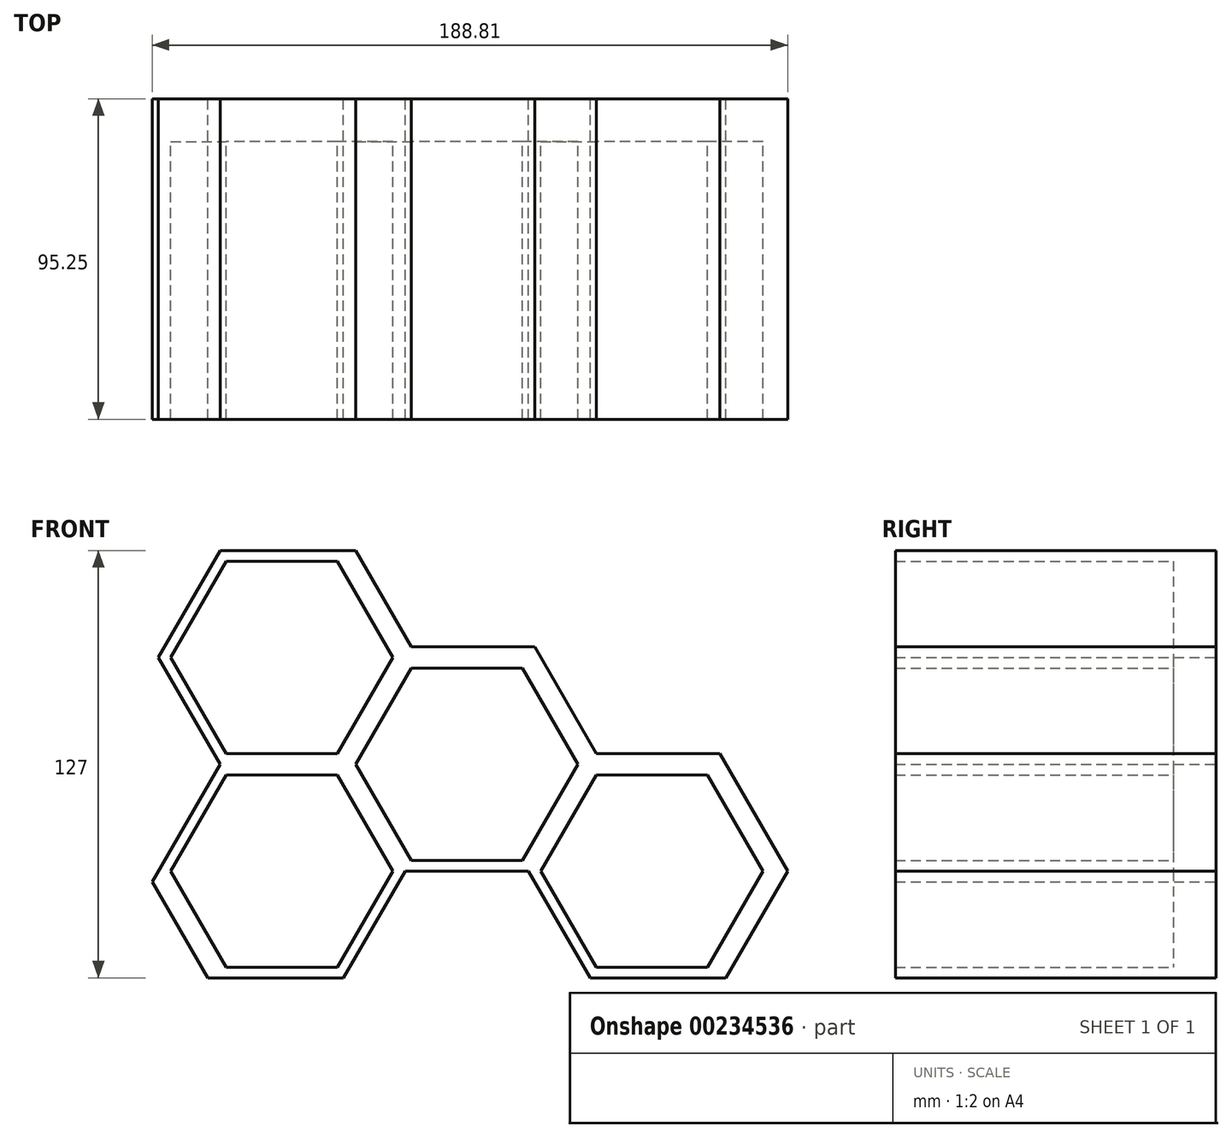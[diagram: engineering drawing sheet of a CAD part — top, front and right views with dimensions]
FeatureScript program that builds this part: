
annotation { "Feature Type Name" : "Feature", "Feature Type Description" : "" }
export const myFeature = defineFeature(function(context is Context, id is Id, definition is map)
    precondition{}
    {
        {
            var Q0;
            Q0=qCreatedBy(makeId("Front.planeOp"),FACE);
            var sketch = newSketch(context, id + "F0", { "sketchPlane" : qUnion([Q0])});
            skLineSegment(sketch, "E0.2", {"start": v(32.38, 98.54) * mm, "end": v(50.71, 66.8) * mm});
            skLineSegment(sketch, "E0.3", {"start": v(50.71, 66.8) * mm, "end": v(32.38, 35.04) * mm});
            skLineSegment(sketch, "E1.3", {"start": v(50.71, 130.3) * mm, "end": v(32.38, 98.54) * mm});
            skLineSegment(sketch, "E2.4", {"start": v(87.38, 130.3) * mm, "end": v(50.71, 130.3) * mm});
            skCircle(sketch, "E3.cCircle", {"center": v(69.05, 98.54) * mm, "radius": 28.58 * mm, "construction": true});
            skLineSegment(sketch, "E3.0", {"start": v(36.05, 98.54) * mm, "end": v(52.55, 127.12) * mm});
            skLineSegment(sketch, "E3.1", {"start": v(52.55, 127.12) * mm, "end": v(85.54, 127.12) * mm});
            skLineSegment(sketch, "E3.2", {"start": v(85.54, 127.12) * mm, "end": v(102.04, 98.54) * mm});
            skLineSegment(sketch, "E3.3", {"start": v(102.04, 98.54) * mm, "end": v(85.54, 69.97) * mm});
            skLineSegment(sketch, "E3.4", {"start": v(85.54, 69.97) * mm, "end": v(52.55, 69.97) * mm});
            skLineSegment(sketch, "E3.5", {"start": v(52.55, 69.97) * mm, "end": v(36.05, 98.54) * mm});
            skPoint(sketch, "E3.0.midPoint", {"position": v(44.3, 112.83) * mm});
            skCircle(sketch, "E4.cCircle", {"center": v(69.05, 98.54) * mm, "radius": 31.75 * mm, "construction": true});
            skLineSegment(sketch, "E4.0", {"start": v(32.38, 98.54) * mm, "end": v(50.71, 130.3) * mm});
            skLineSegment(sketch, "E4.1", {"start": v(50.71, 130.3) * mm, "end": v(87.38, 130.3) * mm});
            skLineSegment(sketch, "E4.2", {"start": v(87.38, 130.3) * mm, "end": v(105.7, 98.54) * mm});
            skLineSegment(sketch, "E4.3", {"start": v(105.7, 98.54) * mm, "end": v(87.38, 66.8) * mm});
            skLineSegment(sketch, "E4.4", {"start": v(87.38, 66.8) * mm, "end": v(50.71, 66.8) * mm});
            skLineSegment(sketch, "E4.5", {"start": v(50.71, 66.8) * mm, "end": v(32.38, 98.54) * mm});
            skPoint(sketch, "E4.0.midPoint", {"position": v(41.55, 114.42) * mm});
            skCircle(sketch, "E5.cCircle", {"center": v(69.05, 35.04) * mm, "radius": 28.58 * mm, "construction": true});
            skLineSegment(sketch, "E5.0", {"start": v(36.05, 35.04) * mm, "end": v(52.55, 63.62) * mm});
            skLineSegment(sketch, "E5.1", {"start": v(52.55, 63.62) * mm, "end": v(85.54, 63.62) * mm});
            skLineSegment(sketch, "E5.2", {"start": v(85.54, 63.62) * mm, "end": v(102.04, 35.04) * mm});
            skLineSegment(sketch, "E5.3", {"start": v(102.04, 35.04) * mm, "end": v(85.54, 6.47) * mm});
            skLineSegment(sketch, "E5.4", {"start": v(85.54, 6.47) * mm, "end": v(52.55, 6.47) * mm});
            skLineSegment(sketch, "E5.5", {"start": v(52.55, 6.47) * mm, "end": v(36.05, 35.04) * mm});
            skPoint(sketch, "E5.0.midPoint", {"position": v(44.3, 49.33) * mm});
            skCircle(sketch, "E6.cCircle", {"center": v(69.05, 35.04) * mm, "radius": 31.75 * mm, "construction": true});
            skLineSegment(sketch, "E6.0", {"start": v(32.38, 35.04) * mm, "end": v(50.71, 66.8) * mm});
            skLineSegment(sketch, "E6.1", {"start": v(50.71, 66.8) * mm, "end": v(87.38, 66.8) * mm});
            skLineSegment(sketch, "E6.2", {"start": v(87.38, 66.8) * mm, "end": v(105.7, 35.04) * mm});
            skLineSegment(sketch, "E6.3", {"start": v(105.7, 35.04) * mm, "end": v(87.38, 3.3) * mm});
            skLineSegment(sketch, "E6.4", {"start": v(87.38, 3.3) * mm, "end": v(50.71, 3.3) * mm});
            skLineSegment(sketch, "E6.5", {"start": v(50.71, 3.3) * mm, "end": v(32.38, 35.04) * mm});
            skPoint(sketch, "E6.0.midPoint", {"position": v(41.55, 50.92) * mm});
            skLineSegment(sketch, "E7.1", {"start": v(50.71, 3.3) * mm, "end": v(87.38, 3.3) * mm});
            skLineSegment(sketch, "E8.0", {"start": v(87.38, 3.3) * mm, "end": v(105.7, 35.04) * mm});
            skLineSegment(sketch, "E8.1", {"start": v(105.7, 35.04) * mm, "end": v(142.37, 35.04) * mm});
            skLineSegment(sketch, "E8.2", {"start": v(142.37, 35.04) * mm, "end": v(160.7, 3.3) * mm});
            skPoint(sketch, "E8.0.midPoint", {"position": v(96.54, 19.17) * mm});
            skCircle(sketch, "E9.cCircle", {"center": v(124.04, 66.8) * mm, "radius": 28.58 * mm, "construction": true});
            skLineSegment(sketch, "E9.0", {"start": v(91.04, 66.8) * mm, "end": v(107.54, 95.37) * mm});
            skLineSegment(sketch, "E9.1", {"start": v(107.54, 95.37) * mm, "end": v(140.54, 95.37) * mm});
            skLineSegment(sketch, "E9.2", {"start": v(140.54, 95.37) * mm, "end": v(157.03, 66.8) * mm});
            skLineSegment(sketch, "E9.3", {"start": v(157.03, 66.8) * mm, "end": v(140.54, 38.22) * mm});
            skLineSegment(sketch, "E9.4", {"start": v(140.54, 38.22) * mm, "end": v(107.54, 38.22) * mm});
            skLineSegment(sketch, "E9.5", {"start": v(107.54, 38.22) * mm, "end": v(91.04, 66.8) * mm});
            skPoint(sketch, "E9.0.midPoint", {"position": v(99.3, 81.08) * mm});
            skCircle(sketch, "E10.cCircle", {"center": v(124.04, 66.8) * mm, "radius": 31.75 * mm, "construction": true});
            skLineSegment(sketch, "E10.0", {"start": v(87.38, 66.8) * mm, "end": v(105.7, 98.54) * mm});
            skLineSegment(sketch, "E10.1", {"start": v(105.7, 98.54) * mm, "end": v(142.37, 98.54) * mm});
            skLineSegment(sketch, "E10.2", {"start": v(142.37, 98.54) * mm, "end": v(160.7, 66.8) * mm});
            skLineSegment(sketch, "E10.3", {"start": v(160.7, 66.8) * mm, "end": v(142.37, 35.04) * mm});
            skLineSegment(sketch, "E10.4", {"start": v(142.37, 35.04) * mm, "end": v(105.7, 35.04) * mm});
            skLineSegment(sketch, "E10.5", {"start": v(105.7, 35.04) * mm, "end": v(87.38, 66.8) * mm});
            skPoint(sketch, "E10.0.midPoint", {"position": v(96.54, 82.67) * mm});
            skLineSegment(sketch, "E11.1", {"start": v(160.7, 3.3) * mm, "end": v(197.36, 3.3) * mm});
            skCircle(sketch, "E12.cCircle", {"center": v(179.03, 35.04) * mm, "radius": 28.58 * mm, "construction": true});
            skLineSegment(sketch, "E12.0", {"start": v(146.03, 35.04) * mm, "end": v(162.53, 63.62) * mm});
            skLineSegment(sketch, "E12.1", {"start": v(162.53, 63.62) * mm, "end": v(195.53, 63.62) * mm});
            skLineSegment(sketch, "E12.2", {"start": v(195.53, 63.62) * mm, "end": v(212.03, 35.04) * mm});
            skLineSegment(sketch, "E12.3", {"start": v(212.03, 35.04) * mm, "end": v(195.53, 6.47) * mm});
            skLineSegment(sketch, "E12.4", {"start": v(195.53, 6.47) * mm, "end": v(162.53, 6.47) * mm});
            skLineSegment(sketch, "E12.5", {"start": v(162.53, 6.47) * mm, "end": v(146.03, 35.04) * mm});
            skPoint(sketch, "E12.0.midPoint", {"position": v(154.28, 49.33) * mm});
            skCircle(sketch, "E13.cCircle", {"center": v(179.03, 35.04) * mm, "radius": 31.75 * mm, "construction": true});
            skLineSegment(sketch, "E13.0", {"start": v(142.37, 35.04) * mm, "end": v(160.7, 66.8) * mm});
            skLineSegment(sketch, "E13.1", {"start": v(160.7, 66.8) * mm, "end": v(197.36, 66.8) * mm});
            skLineSegment(sketch, "E13.2", {"start": v(197.36, 66.8) * mm, "end": v(215.7, 35.04) * mm});
            skLineSegment(sketch, "E13.3", {"start": v(215.7, 35.04) * mm, "end": v(197.36, 3.3) * mm});
            skLineSegment(sketch, "E13.4", {"start": v(197.36, 3.3) * mm, "end": v(160.7, 3.3) * mm});
            skLineSegment(sketch, "E13.5", {"start": v(160.7, 3.3) * mm, "end": v(142.37, 35.04) * mm});
            skPoint(sketch, "E13.0.midPoint", {"position": v(151.53, 50.92) * mm});
            skLineSegment(sketch, "E14", {"start": v(30.55, 31.87) * mm, "end": v(47.05, 3.3) * mm});
            skLineSegment(sketch, "E15", {"start": v(201.03, 3.3) * mm, "end": v(219.36, 35.04) * mm});
            skLineSegment(sketch, "E16", {"start": v(219.36, 35.04) * mm, "end": v(199.2, 69.97) * mm});
            skLineSegment(sketch, "E17", {"start": v(199.2, 69.97) * mm, "end": v(162.53, 69.97) * mm});
            skLineSegment(sketch, "E18", {"start": v(162.53, 69.97) * mm, "end": v(144.2, 101.72) * mm});
            skLineSegment(sketch, "E19", {"start": v(144.2, 101.72) * mm, "end": v(107.54, 101.72) * mm});
            skLineSegment(sketch, "E20", {"start": v(107.54, 101.72) * mm, "end": v(91.04, 130.3) * mm});
            skLineSegment(sketch, "E21", {"start": v(47.05, 3.3) * mm, "end": v(50.71, 3.3) * mm});
            skLineSegment(sketch, "E22", {"start": v(32.38, 35.04) * mm, "end": v(30.55, 31.87) * mm});
            skLineSegment(sketch, "E23", {"start": v(91.04, 130.3) * mm, "end": v(87.38, 130.3) * mm});
            skLineSegment(sketch, "E24", {"start": v(201.03, 3.3) * mm, "end": v(197.36, 3.3) * mm});
            skSolve(sketch);
        }
        {
            var Q0;
            Q0=makeQuery(id+"F0.imprint","IMPRINT",FACE,{"disambiguationData":[TD([[makeQuery(id+"F0.imprint","IMPRINT",EDGE,{"derivedFrom":sQuery(id+"F0.wireOp",EDGE,"68d16a58-0471-4e1c-b2b3-2a61df7c0d9d.0")}),-1.0]])]});
            var Q1;
            Q1=makeQuery(id+"F0.imprint","IMPRINT",FACE,{"disambiguationData":[TD([[makeQuery(id+"F0.imprint","IMPRINT",EDGE,{"derivedFrom":sQuery(id+"F0.wireOp",EDGE,"ae29455d-c252-400a-b569-c5a1c48e1351.0")}),-1.0]])]});
            var Q2;
            Q2=makeQuery(id+"F0.imprint","IMPRINT",FACE,{"disambiguationData":[TD([[makeQuery(id+"F0.imprint","IMPRINT",EDGE,{"derivedFrom":sQuery(id+"F0.wireOp",EDGE,"cad1e4f3-bd43-45ec-b31a-1d5006939c94.0")}),-1.0]])]});
            var Q3;
            Q3=makeQuery(id+"F0.imprint","IMPRINT",FACE,{"disambiguationData":[TD([[makeQuery(id+"F0.imprint","IMPRINT",EDGE,{"derivedFrom":sQuery(id+"F0.wireOp",EDGE,"b43d4d8c-f78a-4ff8-8565-99a66ce6ec5f.0")}),-1.0]])]});
            var Q4;
            Q4=makeQuery(id+"F0.imprint","IMPRINT",FACE,{"disambiguationData":[TD([[makeQuery(id+"F0.imprint","IMPRINT",EDGE,{"derivedFrom":sQuery(id+"F0.wireOp",EDGE,"E3.0")}),-1.0]])]});
            var Q5;
            Q5=makeQuery(id+"F0.imprint","IMPRINT",FACE,{"disambiguationData":[TD([[makeQuery(id+"F0.imprint","IMPRINT",EDGE,{"derivedFrom":sQuery(id+"F0.wireOp",EDGE,"E5.0")}),-1.0]])]});
            var Q6;
            Q6=makeQuery(id+"F0.imprint","IMPRINT",FACE,{"disambiguationData":[TD([[makeQuery(id+"F0.imprint","IMPRINT",EDGE,{"derivedFrom":sQuery(id+"F0.wireOp",EDGE,"0bf0733b-7d93-4c2e-8366-56d2cde24658.0")}),-1.0]])]});
            var Q7;
            Q7=makeQuery(id+"F0.imprint","IMPRINT",FACE,{"disambiguationData":[TD([[makeQuery(id+"F0.imprint","IMPRINT",EDGE,{"derivedFrom":sQuery(id+"F0.wireOp",EDGE,"93717492-86db-456f-ae55-f71e4e93837b.0")}),-1.0]])]});
            var Q8;
            Q8=makeQuery(id+"F0.imprint","IMPRINT",FACE,{"disambiguationData":[TD([[makeQuery(id+"F0.imprint","IMPRINT",EDGE,{"derivedFrom":sQuery(id+"F0.wireOp",EDGE,"f16ea8c9-6b67-4651-8441-f7eb3c0ce7d7.0")}),-1.0]])]});
            var Q9;
            Q9=makeQuery(id+"F0.imprint","IMPRINT",FACE,{"disambiguationData":[TD([[makeQuery(id+"F0.imprint","IMPRINT",EDGE,{"derivedFrom":sQuery(id+"F0.wireOp",EDGE,"0306a0a6-7289-4661-a415-5fa5585f2cb5.0")}),-1.0]])]});
            var Q10;
            Q10=makeQuery(id+"F0.imprint","IMPRINT",FACE,{"disambiguationData":[TD([[makeQuery(id+"F0.imprint","IMPRINT",EDGE,{"derivedFrom":sQuery(id+"F0.wireOp",EDGE,"0a91a14e-ea0c-483f-91eb-c48bd73cb0e6.0")}),-1.0]])]});
            var Q11;
            Q11=makeQuery(id+"F0.imprint","IMPRINT",FACE,{"disambiguationData":[TD([[makeQuery(id+"F0.imprint","IMPRINT",EDGE,{"derivedFrom":sQuery(id+"F0.wireOp",EDGE,"cbfd9497-f7fe-4f18-9288-d90aa8075d81.0")}),-1.0]])]});
            var Q12;
            Q12=makeQuery(id+"F0.imprint","IMPRINT",FACE,{"disambiguationData":[TD([[makeQuery(id+"F0.imprint","IMPRINT",EDGE,{"derivedFrom":sQuery(id+"F0.wireOp",EDGE,"6282d196-dd8f-4bb0-bca4-b9108e277473.0")}),-1.0]])]});
            var Q13;
            Q13=makeQuery(id+"F0.imprint","IMPRINT",FACE,{"disambiguationData":[TD([[makeQuery(id+"F0.imprint","IMPRINT",EDGE,{"derivedFrom":sQuery(id+"F0.wireOp",EDGE,"084ca30c-4dc0-463f-bfd9-557787ed9a2f.0")}),-1.0]])]});
            var Q14;
            Q14=makeQuery(id+"F0.imprint","IMPRINT",FACE,{"disambiguationData":[TD([[makeQuery(id+"F0.imprint","IMPRINT",EDGE,{"derivedFrom":sQuery(id+"F0.wireOp",EDGE,"E12.0")}),-1.0]])]});
            var Q15;
            Q15=makeQuery(id+"F0.imprint","IMPRINT",FACE,{"disambiguationData":[TD([[makeQuery(id+"F0.imprint","IMPRINT",EDGE,{"derivedFrom":sQuery(id+"F0.wireOp",EDGE,"b8eec94e-d97e-439b-aaac-63499233db4c.0")}),-1.0]])]});
            var Q16;
            Q16=makeQuery(id+"F0.imprint","IMPRINT",FACE,{"disambiguationData":[TD([[makeQuery(id+"F0.imprint","IMPRINT",EDGE,{"derivedFrom":sQuery(id+"F0.wireOp",EDGE,"2e929887-9bb9-4083-9cef-f9a6a24e8e46.0")}),-1.0]])]});
            var Q17;
            Q17=makeQuery(id+"F0.imprint","IMPRINT",FACE,{"disambiguationData":[TD([[makeQuery(id+"F0.imprint","IMPRINT",EDGE,{"derivedFrom":sQuery(id+"F0.wireOp",EDGE,"23671680-92ab-419e-a071-eb0943a5012b.0")}),-1.0]])]});
            var Q18;
            Q18=makeQuery(id+"F0.imprint","IMPRINT",FACE,{"disambiguationData":[TD([[makeQuery(id+"F0.imprint","IMPRINT",EDGE,{"derivedFrom":sQuery(id+"F0.wireOp",EDGE,"a1daa6ae-7864-4614-8fb9-3511dddc1266.0")}),-1.0]])]});
            var Q19;
            Q19=makeQuery(id+"F0.imprint","IMPRINT",FACE,{"disambiguationData":[TD([[makeQuery(id+"F0.imprint","IMPRINT",EDGE,{"derivedFrom":sQuery(id+"F0.wireOp",EDGE,"37efd634-c264-4683-8864-08b38c7986ca.0")}),-1.0]])]});
            var Q20;
            Q20=makeQuery(id+"F0.imprint","IMPRINT",FACE,{"disambiguationData":[TD([[makeQuery(id+"F0.imprint","IMPRINT",EDGE,{"derivedFrom":sQuery(id+"F0.wireOp",EDGE,"E9.0")}),-1.0]])]});
            var Q21;
            Q21=makeQuery(id+"F0.imprint","IMPRINT",FACE,{"disambiguationData":[TD([[makeQuery(id+"F0.imprint","IMPRINT",EDGE,{"derivedFrom":sQuery(id+"F0.wireOp",EDGE,"1f2aec04-a318-49b9-a42e-ea2fce35ed6c.0")}),-1.0]])]});
            var Q22;
            Q22=makeQuery(id+"F0.imprint","IMPRINT",FACE,{"disambiguationData":[TD([[makeQuery(id+"F0.imprint","IMPRINT",EDGE,{"derivedFrom":sQuery(id+"F0.wireOp",EDGE,"f97fdbdd-69fc-44f1-b8f7-f6a6a25558e6.0")}),-1.0]])]});
            var Q23;
            Q23=makeQuery(id+"F0.imprint","IMPRINT",FACE,{"disambiguationData":[TD([[makeQuery(id+"F0.imprint","IMPRINT",EDGE,{"derivedFrom":sQuery(id+"F0.wireOp",EDGE,"4e92e904-9607-490d-a429-b319c41500d9.0")}),-1.0]])]});
            var Q24;
            Q24=makeQuery(id+"F0.imprint","IMPRINT",FACE,{"disambiguationData":[TD([[makeQuery(id+"F0.imprint","IMPRINT",EDGE,{"derivedFrom":sQuery(id+"F0.wireOp",EDGE,"084ca30c-4dc0-463f-bfd9-557787ed9a2f.0")}),1.0]])]});
            var Q25;
            Q25=makeQuery(id+"F0.imprint","IMPRINT",FACE,{"disambiguationData":[TD([[makeQuery(id+"F0.imprint","IMPRINT",EDGE,{"derivedFrom":sQuery(id+"F0.wireOp",EDGE,"1f2aec04-a318-49b9-a42e-ea2fce35ed6c.0")}),1.0]])]});
            var Q26;
            Q26=makeQuery(id+"F0.imprint","IMPRINT",FACE,{"disambiguationData":[TD([[makeQuery(id+"F0.imprint","IMPRINT",EDGE,{"derivedFrom":sQuery(id+"F0.wireOp",EDGE,"23671680-92ab-419e-a071-eb0943a5012b.0")}),1.0]])]});
            var Q27;
            Q27=makeQuery(id+"F0.imprint","IMPRINT",FACE,{"disambiguationData":[TD([[makeQuery(id+"F0.imprint","IMPRINT",EDGE,{"derivedFrom":sQuery(id+"F0.wireOp",EDGE,"2e929887-9bb9-4083-9cef-f9a6a24e8e46.0")}),1.0]])]});
            var Q28;
            Q28=makeQuery(id+"F0.imprint","IMPRINT",FACE,{"disambiguationData":[TD([[makeQuery(id+"F0.imprint","IMPRINT",EDGE,{"derivedFrom":sQuery(id+"F0.wireOp",EDGE,"4e92e904-9607-490d-a429-b319c41500d9.0")}),1.0]])]});
            var Q29;
            Q29=makeQuery(id+"F0.imprint","IMPRINT",FACE,{"disambiguationData":[TD([[makeQuery(id+"F0.imprint","IMPRINT",EDGE,{"derivedFrom":sQuery(id+"F0.wireOp",EDGE,"b43d4d8c-f78a-4ff8-8565-99a66ce6ec5f.0")}),1.0]])]});
            var Q30;
            Q30=makeQuery(id+"F0.imprint","IMPRINT",FACE,{"disambiguationData":[TD([[makeQuery(id+"F0.imprint","IMPRINT",EDGE,{"derivedFrom":sQuery(id+"F0.wireOp",EDGE,"ae29455d-c252-400a-b569-c5a1c48e1351.0")}),1.0]])]});
            var Q31;
            Q31=makeQuery(id+"F0.imprint","IMPRINT",FACE,{"disambiguationData":[TD([[makeQuery(id+"F0.imprint","IMPRINT",EDGE,{"derivedFrom":sQuery(id+"F0.wireOp",EDGE,"0a91a14e-ea0c-483f-91eb-c48bd73cb0e6.0")}),1.0]])]});
            var Q32;
            Q32=makeQuery(id+"F0.imprint","IMPRINT",FACE,{"disambiguationData":[TD([[makeQuery(id+"F0.imprint","IMPRINT",EDGE,{"derivedFrom":sQuery(id+"F0.wireOp",EDGE,"E5.0")}),1.0]])]});
            var Q33;
            Q33=makeQuery(id+"F0.imprint","IMPRINT",FACE,{"disambiguationData":[TD([[makeQuery(id+"F0.imprint","IMPRINT",EDGE,{"derivedFrom":sQuery(id+"F0.wireOp",EDGE,"cbfd9497-f7fe-4f18-9288-d90aa8075d81.0")}),1.0]])]});
            var Q34;
            Q34=makeQuery(id+"F0.imprint","IMPRINT",FACE,{"disambiguationData":[TD([[makeQuery(id+"F0.imprint","IMPRINT",EDGE,{"derivedFrom":sQuery(id+"F0.wireOp",EDGE,"f97fdbdd-69fc-44f1-b8f7-f6a6a25558e6.0")}),1.0]])]});
            var Q35;
            Q35=makeQuery(id+"F0.imprint","IMPRINT",FACE,{"disambiguationData":[TD([[makeQuery(id+"F0.imprint","IMPRINT",EDGE,{"derivedFrom":sQuery(id+"F0.wireOp",EDGE,"b8eec94e-d97e-439b-aaac-63499233db4c.0")}),1.0]])]});
            var Q36;
            Q36=makeQuery(id+"F0.imprint","IMPRINT",FACE,{"disambiguationData":[TD([[makeQuery(id+"F0.imprint","IMPRINT",EDGE,{"derivedFrom":sQuery(id+"F0.wireOp",EDGE,"E3.0")}),1.0]])]});
            var Q37;
            Q37=makeQuery(id+"F0.imprint","IMPRINT",FACE,{"disambiguationData":[TD([[makeQuery(id+"F0.imprint","IMPRINT",EDGE,{"derivedFrom":sQuery(id+"F0.wireOp",EDGE,"f16ea8c9-6b67-4651-8441-f7eb3c0ce7d7.0")}),1.0]])]});
            var Q38;
            Q38=makeQuery(id+"F0.imprint","IMPRINT",FACE,{"disambiguationData":[TD([[makeQuery(id+"F0.imprint","IMPRINT",EDGE,{"derivedFrom":sQuery(id+"F0.wireOp",EDGE,"37efd634-c264-4683-8864-08b38c7986ca.0")}),1.0]])]});
            var Q39;
            Q39=makeQuery(id+"F0.imprint","IMPRINT",FACE,{"disambiguationData":[TD([[makeQuery(id+"F0.imprint","IMPRINT",EDGE,{"derivedFrom":sQuery(id+"F0.wireOp",EDGE,"68d16a58-0471-4e1c-b2b3-2a61df7c0d9d.0")}),1.0]])]});
            var Q40;
            Q40=makeQuery(id+"F0.imprint","IMPRINT",FACE,{"disambiguationData":[TD([[makeQuery(id+"F0.imprint","IMPRINT",EDGE,{"derivedFrom":sQuery(id+"F0.wireOp",EDGE,"0306a0a6-7289-4661-a415-5fa5585f2cb5.0")}),1.0]])]});
            var Q41;
            Q41=makeQuery(id+"F0.imprint","IMPRINT",FACE,{"disambiguationData":[TD([[makeQuery(id+"F0.imprint","IMPRINT",EDGE,{"derivedFrom":sQuery(id+"F0.wireOp",EDGE,"0bf0733b-7d93-4c2e-8366-56d2cde24658.0")}),1.0]])]});
            var Q42;
            Q42=makeQuery(id+"F0.imprint","IMPRINT",FACE,{"disambiguationData":[TD([[makeQuery(id+"F0.imprint","IMPRINT",EDGE,{"derivedFrom":sQuery(id+"F0.wireOp",EDGE,"E12.0")}),1.0]])]});
            var Q43;
            Q43=makeQuery(id+"F0.imprint","IMPRINT",FACE,{"disambiguationData":[TD([[makeQuery(id+"F0.imprint","IMPRINT",EDGE,{"derivedFrom":sQuery(id+"F0.wireOp",EDGE,"6282d196-dd8f-4bb0-bca4-b9108e277473.0")}),1.0]])]});
            var Q44;
            Q44=makeQuery(id+"F0.imprint","IMPRINT",FACE,{"disambiguationData":[TD([[makeQuery(id+"F0.imprint","IMPRINT",EDGE,{"derivedFrom":sQuery(id+"F0.wireOp",EDGE,"cad1e4f3-bd43-45ec-b31a-1d5006939c94.0")}),1.0]])]});
            var Q45;
            Q45=makeQuery(id+"F0.imprint","IMPRINT",FACE,{"disambiguationData":[TD([[makeQuery(id+"F0.imprint","IMPRINT",EDGE,{"derivedFrom":sQuery(id+"F0.wireOp",EDGE,"E9.0")}),1.0]])]});
            var Q46;
            Q46=makeQuery(id+"F0.imprint","IMPRINT",FACE,{"disambiguationData":[TD([[makeQuery(id+"F0.imprint","IMPRINT",EDGE,{"derivedFrom":sQuery(id+"F0.wireOp",EDGE,"a1daa6ae-7864-4614-8fb9-3511dddc1266.0")}),1.0]])]});
            var Q47;
            Q47=makeQuery(id+"F0.imprint","IMPRINT",FACE,{"disambiguationData":[TD([[makeQuery(id+"F0.imprint","IMPRINT",EDGE,{"derivedFrom":sQuery(id+"F0.wireOp",EDGE,"93717492-86db-456f-ae55-f71e4e93837b.0")}),1.0]])]});
            extrude(context, id + "F1", {"entities" : qUnion([Q0, Q1, Q2, Q3, Q4, Q5, Q6, Q7, Q8, Q9, Q10, Q11, Q12, Q13, Q14, Q15, Q16, Q17, Q18, Q19, Q20, Q21, Q22, Q23, Q24, Q25, Q26, Q27, Q28, Q29, Q30, Q31, Q32, Q33, Q34, Q35, Q36, Q37, Q38, Q39, Q40, Q41, Q42, Q43, Q44, Q45, Q46, Q47]), "depth" : 12.7 * mm});
        }
        {
            var Q0;
            Q0=makeQuery(id+"F0.imprint","IMPRINT",FACE,{"disambiguationData":[TD([[makeQuery(id+"F0.imprint","IMPRINT",EDGE,{"derivedFrom":sQuery(id+"F0.wireOp",EDGE,"E3.0")}),1.0]])]});
            var Q1;
            Q1=makeQuery(id+"F0.imprint","IMPRINT",FACE,{"disambiguationData":[TD([[makeQuery(id+"F0.imprint","IMPRINT",EDGE,{"derivedFrom":sQuery(id+"F0.wireOp",EDGE,"b8eec94e-d97e-439b-aaac-63499233db4c.0")}),1.0]])]});
            var Q2;
            Q2=makeQuery(id+"F0.imprint","IMPRINT",FACE,{"disambiguationData":[TD([[makeQuery(id+"F0.imprint","IMPRINT",EDGE,{"derivedFrom":sQuery(id+"F0.wireOp",EDGE,"cad1e4f3-bd43-45ec-b31a-1d5006939c94.0")}),1.0]])]});
            var Q3;
            Q3=makeQuery(id+"F0.imprint","IMPRINT",FACE,{"disambiguationData":[TD([[makeQuery(id+"F0.imprint","IMPRINT",EDGE,{"derivedFrom":sQuery(id+"F0.wireOp",EDGE,"68d16a58-0471-4e1c-b2b3-2a61df7c0d9d.0")}),1.0]])]});
            var Q4;
            Q4=makeQuery(id+"F0.imprint","IMPRINT",FACE,{"disambiguationData":[TD([[makeQuery(id+"F0.imprint","IMPRINT",EDGE,{"derivedFrom":sQuery(id+"F0.wireOp",EDGE,"0306a0a6-7289-4661-a415-5fa5585f2cb5.0")}),1.0]])]});
            var Q5;
            Q5=makeQuery(id+"F0.imprint","IMPRINT",FACE,{"disambiguationData":[TD([[makeQuery(id+"F0.imprint","IMPRINT",EDGE,{"derivedFrom":sQuery(id+"F0.wireOp",EDGE,"084ca30c-4dc0-463f-bfd9-557787ed9a2f.0")}),1.0]])]});
            var Q6;
            Q6=makeQuery(id+"F0.imprint","IMPRINT",FACE,{"disambiguationData":[TD([[makeQuery(id+"F0.imprint","IMPRINT",EDGE,{"derivedFrom":sQuery(id+"F0.wireOp",EDGE,"4e92e904-9607-490d-a429-b319c41500d9.0")}),1.0]])]});
            var Q7;
            Q7=makeQuery(id+"F0.imprint","IMPRINT",FACE,{"disambiguationData":[TD([[makeQuery(id+"F0.imprint","IMPRINT",EDGE,{"derivedFrom":sQuery(id+"F0.wireOp",EDGE,"a1daa6ae-7864-4614-8fb9-3511dddc1266.0")}),1.0]])]});
            var Q8;
            Q8=makeQuery(id+"F0.imprint","IMPRINT",FACE,{"disambiguationData":[TD([[makeQuery(id+"F0.imprint","IMPRINT",EDGE,{"derivedFrom":sQuery(id+"F0.wireOp",EDGE,"93717492-86db-456f-ae55-f71e4e93837b.0")}),1.0]])]});
            var Q9;
            Q9=makeQuery(id+"F0.imprint","IMPRINT",FACE,{"disambiguationData":[TD([[makeQuery(id+"F0.imprint","IMPRINT",EDGE,{"derivedFrom":sQuery(id+"F0.wireOp",EDGE,"E5.0")}),1.0]])]});
            var Q10;
            Q10=makeQuery(id+"F0.imprint","IMPRINT",FACE,{"disambiguationData":[TD([[makeQuery(id+"F0.imprint","IMPRINT",EDGE,{"derivedFrom":sQuery(id+"F0.wireOp",EDGE,"E9.0")}),1.0]])]});
            var Q11;
            Q11=makeQuery(id+"F0.imprint","IMPRINT",FACE,{"disambiguationData":[TD([[makeQuery(id+"F0.imprint","IMPRINT",EDGE,{"derivedFrom":sQuery(id+"F0.wireOp",EDGE,"23671680-92ab-419e-a071-eb0943a5012b.0")}),1.0]])]});
            var Q12;
            Q12=makeQuery(id+"F0.imprint","IMPRINT",FACE,{"disambiguationData":[TD([[makeQuery(id+"F0.imprint","IMPRINT",EDGE,{"derivedFrom":sQuery(id+"F0.wireOp",EDGE,"E12.0")}),1.0]])]});
            var Q13;
            Q13=makeQuery(id+"F0.imprint","IMPRINT",FACE,{"disambiguationData":[TD([[makeQuery(id+"F0.imprint","IMPRINT",EDGE,{"derivedFrom":sQuery(id+"F0.wireOp",EDGE,"ae29455d-c252-400a-b569-c5a1c48e1351.0")}),1.0]])]});
            var Q14;
            Q14=makeQuery(id+"F0.imprint","IMPRINT",FACE,{"disambiguationData":[TD([[makeQuery(id+"F0.imprint","IMPRINT",EDGE,{"derivedFrom":sQuery(id+"F0.wireOp",EDGE,"f97fdbdd-69fc-44f1-b8f7-f6a6a25558e6.0")}),1.0]])]});
            var Q15;
            Q15=makeQuery(id+"F0.imprint","IMPRINT",FACE,{"disambiguationData":[TD([[makeQuery(id+"F0.imprint","IMPRINT",EDGE,{"derivedFrom":sQuery(id+"F0.wireOp",EDGE,"2e929887-9bb9-4083-9cef-f9a6a24e8e46.0")}),1.0]])]});
            var Q16;
            Q16=makeQuery(id+"F0.imprint","IMPRINT",FACE,{"disambiguationData":[TD([[makeQuery(id+"F0.imprint","IMPRINT",EDGE,{"derivedFrom":sQuery(id+"F0.wireOp",EDGE,"0a91a14e-ea0c-483f-91eb-c48bd73cb0e6.0")}),1.0]])]});
            var Q17;
            Q17=makeQuery(id+"F0.imprint","IMPRINT",FACE,{"disambiguationData":[TD([[makeQuery(id+"F0.imprint","IMPRINT",EDGE,{"derivedFrom":sQuery(id+"F0.wireOp",EDGE,"37efd634-c264-4683-8864-08b38c7986ca.0")}),1.0]])]});
            var Q18;
            Q18=makeQuery(id+"F0.imprint","IMPRINT",FACE,{"disambiguationData":[TD([[makeQuery(id+"F0.imprint","IMPRINT",EDGE,{"derivedFrom":sQuery(id+"F0.wireOp",EDGE,"cbfd9497-f7fe-4f18-9288-d90aa8075d81.0")}),1.0]])]});
            var Q19;
            Q19=makeQuery(id+"F0.imprint","IMPRINT",FACE,{"disambiguationData":[TD([[makeQuery(id+"F0.imprint","IMPRINT",EDGE,{"derivedFrom":sQuery(id+"F0.wireOp",EDGE,"6282d196-dd8f-4bb0-bca4-b9108e277473.0")}),1.0]])]});
            var Q20;
            Q20=makeQuery(id+"F0.imprint","IMPRINT",FACE,{"disambiguationData":[TD([[makeQuery(id+"F0.imprint","IMPRINT",EDGE,{"derivedFrom":sQuery(id+"F0.wireOp",EDGE,"0bf0733b-7d93-4c2e-8366-56d2cde24658.0")}),1.0]])]});
            var Q21;
            Q21=makeQuery(id+"F0.imprint","IMPRINT",FACE,{"disambiguationData":[TD([[makeQuery(id+"F0.imprint","IMPRINT",EDGE,{"derivedFrom":sQuery(id+"F0.wireOp",EDGE,"b43d4d8c-f78a-4ff8-8565-99a66ce6ec5f.0")}),1.0]])]});
            var Q22;
            Q22=makeQuery(id+"F0.imprint","IMPRINT",FACE,{"disambiguationData":[TD([[makeQuery(id+"F0.imprint","IMPRINT",EDGE,{"derivedFrom":sQuery(id+"F0.wireOp",EDGE,"f16ea8c9-6b67-4651-8441-f7eb3c0ce7d7.0")}),1.0]])]});
            var Q23;
            Q23=makeQuery(id+"F0.imprint","IMPRINT",FACE,{"disambiguationData":[TD([[makeQuery(id+"F0.imprint","IMPRINT",EDGE,{"derivedFrom":sQuery(id+"F0.wireOp",EDGE,"1f2aec04-a318-49b9-a42e-ea2fce35ed6c.0")}),1.0]])]});
            var Q24;
            {var subQ6=sQuery(id+"F0.wireOp",EDGE,"16495d92-3f2e-4778-aa2a-097d1cd616f4.3");Q24=makeQuery(id+"F0.imprint","IMPRINT",FACE,{"disambiguationData":[TD([[makeQuery(id+"F0.imprint","IMPRINT",EDGE,{"derivedFrom":subQ6}),1.0]])]});}
            var Q25;
            Q25=makeQuery(id+"F0.imprint","IMPRINT",FACE,{"disambiguationData":[TD([[makeQuery(id+"F0.imprint","IMPRINT",EDGE,{"derivedFrom":sQuery(id+"F0.wireOp",EDGE,"16495d92-3f2e-4778-aa2a-097d1cd616f4.1")}),1.0]])]});
            var Q26;
            Q26=makeQuery(id+"F0.imprint","IMPRINT",FACE,{"disambiguationData":[TD([[makeQuery(id+"F0.imprint","IMPRINT",EDGE,{"derivedFrom":sQuery(id+"F0.wireOp",EDGE,"E4.2")}),1.0]])]});
            var Q27;
            Q27=makeQuery(id+"F0.imprint","IMPRINT",FACE,{"disambiguationData":[TD([[makeQuery(id+"F0.imprint","IMPRINT",EDGE,{"derivedFrom":sQuery(id+"F0.wireOp",EDGE,"E6.5")}),1.0]])]});
            extrude(context, id + "F2", {"entities" : qUnion([Q0, Q1, Q2, Q3, Q4, Q5, Q6, Q7, Q8, Q9, Q10, Q11, Q12, Q13, Q14, Q15, Q16, Q17, Q18, Q19, Q20, Q21, Q22, Q23, Q24, Q25, Q26, Q27]), "operationType" : NewBodyOperationType.ADD, "depth" : 95.25 * mm});
        }
    });
